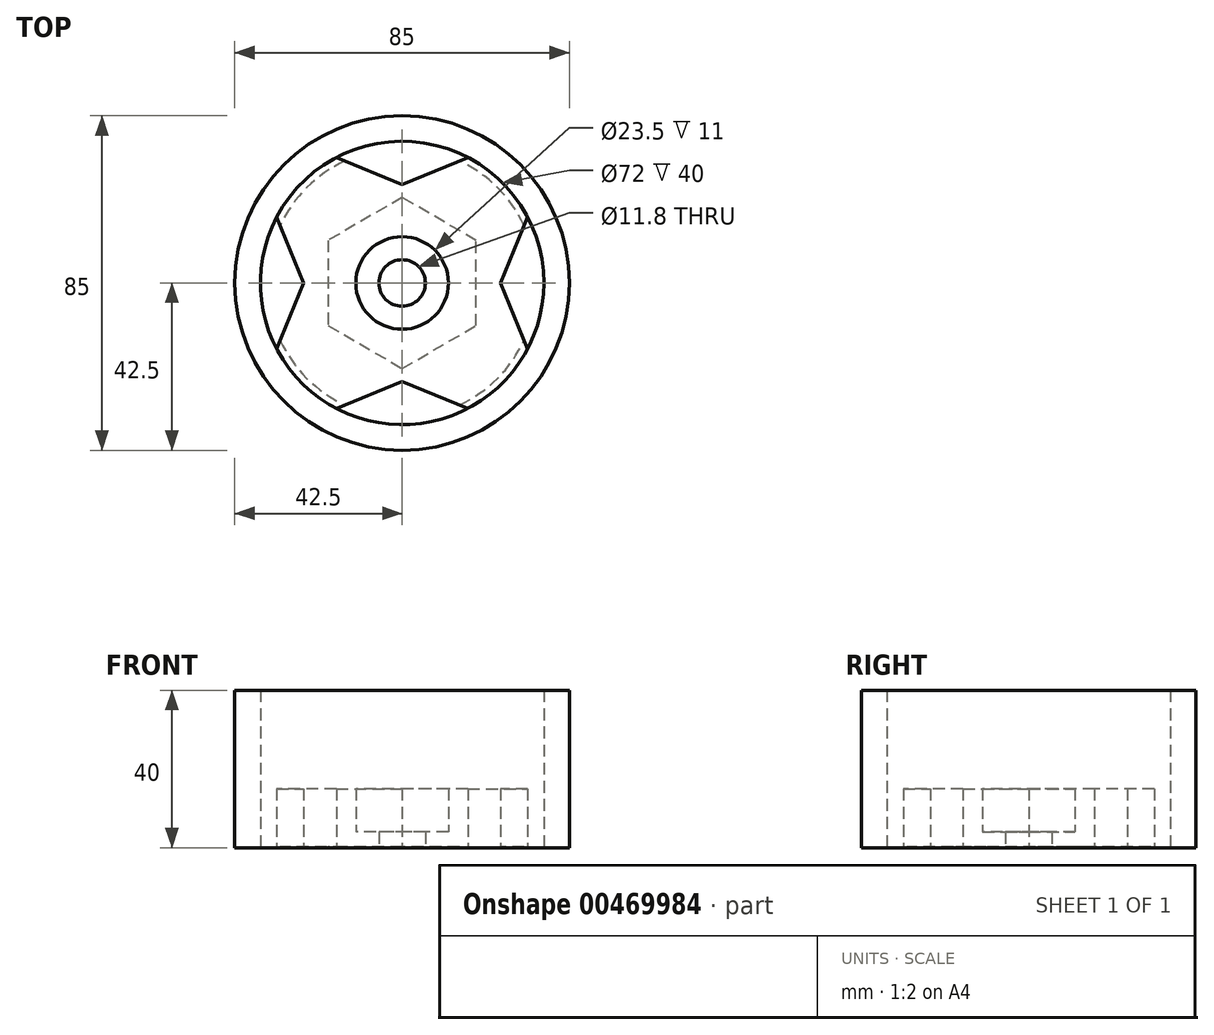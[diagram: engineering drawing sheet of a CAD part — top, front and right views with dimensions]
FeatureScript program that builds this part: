
annotation { "Feature Type Name" : "Feature", "Feature Type Description" : "" }
export const myFeature = defineFeature(function(context is Context, id is Id, definition is map)
    precondition{}
    {
        {
            var Q0;
            Q0=qCreatedBy(makeId("Top.planeOp"),FACE);
            var sketch = newSketch(context, id + "F0", { "sketchPlane" : qUnion([Q0])});
            skCircle(sketch, "E0", {"center": v(0, 0) * mm, "radius": 5.9 * mm});
            skCircle(sketch, "E1", {"center": v(0, 0) * mm, "radius": 11.75 * mm});
            skLineSegment(sketch, "E2.bottom", {"start": v(-42.5, 42.5) * mm, "end": v(42.5, 42.5) * mm, "construction": true});
            skLineSegment(sketch, "E2.top", {"start": v(-42.5, -42.5) * mm, "end": v(42.5, -42.5) * mm, "construction": true});
            skLineSegment(sketch, "E2.left", {"start": v(-42.5, 42.5) * mm, "end": v(-42.5, -42.5) * mm, "construction": true});
            skLineSegment(sketch, "E2.right", {"start": v(42.5, 42.5) * mm, "end": v(42.5, -42.5) * mm, "construction": true});
            skCircle(sketch, "E3.cCircle", {"center": v(0, 0) * mm, "radius": 25 * mm, "construction": true});
            skLineSegment(sketch, "E3.0", {"start": v(-10.35, 25) * mm, "end": v(10.35, 25) * mm, "construction": true});
            skLineSegment(sketch, "E3.1", {"start": v(10.35, 25) * mm, "end": v(25, 10.35) * mm, "construction": true});
            skLineSegment(sketch, "E3.2", {"start": v(25, 10.35) * mm, "end": v(25, -10.35) * mm, "construction": true});
            skLineSegment(sketch, "E3.3", {"start": v(25, -10.35) * mm, "end": v(10.35, -25) * mm, "construction": true});
            skLineSegment(sketch, "E3.4", {"start": v(10.35, -25) * mm, "end": v(-10.35, -25) * mm, "construction": true});
            skLineSegment(sketch, "E3.5", {"start": v(-10.35, -25) * mm, "end": v(-25, -10.35) * mm, "construction": true});
            skLineSegment(sketch, "E3.6", {"start": v(-25, -10.35) * mm, "end": v(-25, 10.35) * mm, "construction": true});
            skLineSegment(sketch, "E3.7", {"start": v(-25, 10.35) * mm, "end": v(-10.35, 25) * mm, "construction": true});
            skPoint(sketch, "E3.0.midPoint", {"position": v(0, 25) * mm});
            skLineSegment(sketch, "E4", {"start": v(-42.5, -42.5) * mm, "end": v(-25, 0) * mm});
            skLineSegment(sketch, "E5", {"start": v(-25, 0) * mm, "end": v(-42.5, 42.5) * mm});
            skLineSegment(sketch, "E6", {"start": v(-42.5, 42.5) * mm, "end": v(0, 25) * mm});
            skLineSegment(sketch, "E7", {"start": v(0, 25) * mm, "end": v(42.5, 42.5) * mm});
            skLineSegment(sketch, "E8", {"start": v(42.5, 42.5) * mm, "end": v(25, 0) * mm});
            skLineSegment(sketch, "E9", {"start": v(25, 0) * mm, "end": v(42.5, -42.5) * mm});
            skLineSegment(sketch, "E10", {"start": v(42.5, -42.5) * mm, "end": v(0, -25) * mm});
            skLineSegment(sketch, "E11", {"start": v(0, -25) * mm, "end": v(-42.5, -42.5) * mm});
            skCircle(sketch, "E12", {"center": v(0, 0) * mm, "radius": 42.5 * mm});
            skCircle(sketch, "E13", {"center": v(0, 0) * mm, "radius": 40 * mm});
            skCircle(sketch, "E14", {"center": v(0, 0) * mm, "radius": 36 * mm});
            skSolve(sketch);
        }
        {
            var Q0;
            {var subQ0=sQuery(id+"F0.wireOp",EDGE,"E12");var subQ1=sQuery(id+"F0.wireOp",EDGE,"E4");var subQ2=makeQuery(id+"F0.imprint","INTERSECT",VERTEX,{"derivedFrom":[subQ1,subQ0]});Q0=makeQuery(id+"F0.imprint","IMPRINT",FACE,{"disambiguationData":[TD([[makeQuery(id+"F0.imprint","IMPRINT",EDGE,{"disambiguationData":[TD([[subQ2,-1.0]])],"derivedFrom":subQ1}),1.0]])]});}
            var Q1;
            {var subQ0=sQuery(id+"F0.wireOp",EDGE,"E12");var subQ1=sQuery(id+"F0.wireOp",EDGE,"E5");var subQ2=makeQuery(id+"F0.imprint","INTERSECT",VERTEX,{"derivedFrom":[subQ1,subQ0]});Q1=makeQuery(id+"F0.imprint","IMPRINT",FACE,{"disambiguationData":[TD([[makeQuery(id+"F0.imprint","IMPRINT",EDGE,{"disambiguationData":[TD([[subQ2,1.0]])],"derivedFrom":subQ1}),-1.0]])]});}
            var Q2;
            {var subQ0=sQuery(id+"F0.wireOp",EDGE,"E12");var subQ1=sQuery(id+"F0.wireOp",EDGE,"E6");var subQ2=makeQuery(id+"F0.imprint","INTERSECT",VERTEX,{"derivedFrom":[subQ1,subQ0]});Q2=makeQuery(id+"F0.imprint","IMPRINT",FACE,{"disambiguationData":[TD([[makeQuery(id+"F0.imprint","IMPRINT",EDGE,{"disambiguationData":[TD([[subQ2,-1.0]])],"derivedFrom":subQ1}),1.0]])]});}
            var Q3;
            {var subQ0=sQuery(id+"F0.wireOp",EDGE,"E12");var subQ1=sQuery(id+"F0.wireOp",EDGE,"E7");var subQ2=makeQuery(id+"F0.imprint","INTERSECT",VERTEX,{"derivedFrom":[subQ1,subQ0]});Q3=makeQuery(id+"F0.imprint","IMPRINT",FACE,{"disambiguationData":[TD([[makeQuery(id+"F0.imprint","IMPRINT",EDGE,{"disambiguationData":[TD([[subQ2,1.0]])],"derivedFrom":subQ1}),-1.0]])]});}
            var Q4;
            {var subQ0=sQuery(id+"F0.wireOp",EDGE,"E12");var subQ1=sQuery(id+"F0.wireOp",EDGE,"E8");var subQ2=makeQuery(id+"F0.imprint","INTERSECT",VERTEX,{"derivedFrom":[subQ1,subQ0]});Q4=makeQuery(id+"F0.imprint","IMPRINT",FACE,{"disambiguationData":[TD([[makeQuery(id+"F0.imprint","IMPRINT",EDGE,{"disambiguationData":[TD([[subQ2,-1.0]])],"derivedFrom":subQ1}),1.0]])]});}
            var Q5;
            {var subQ0=sQuery(id+"F0.wireOp",EDGE,"E12");var subQ1=sQuery(id+"F0.wireOp",EDGE,"E9");var subQ2=makeQuery(id+"F0.imprint","INTERSECT",VERTEX,{"derivedFrom":[subQ1,subQ0]});Q5=makeQuery(id+"F0.imprint","IMPRINT",FACE,{"disambiguationData":[TD([[makeQuery(id+"F0.imprint","IMPRINT",EDGE,{"disambiguationData":[TD([[subQ2,1.0]])],"derivedFrom":subQ1}),-1.0]])]});}
            var Q6;
            {var subQ0=sQuery(id+"F0.wireOp",EDGE,"E12");var subQ1=sQuery(id+"F0.wireOp",EDGE,"E10");var subQ2=makeQuery(id+"F0.imprint","INTERSECT",VERTEX,{"derivedFrom":[subQ1,subQ0]});Q6=makeQuery(id+"F0.imprint","IMPRINT",FACE,{"disambiguationData":[TD([[makeQuery(id+"F0.imprint","IMPRINT",EDGE,{"disambiguationData":[TD([[subQ2,-1.0]])],"derivedFrom":subQ1}),1.0]])]});}
            var Q7;
            {var subQ0=sQuery(id+"F0.wireOp",EDGE,"E12");var subQ1=sQuery(id+"F0.wireOp",EDGE,"E4");var subQ2=makeQuery(id+"F0.imprint","INTERSECT",VERTEX,{"derivedFrom":[subQ1,subQ0]});Q7=makeQuery(id+"F0.imprint","IMPRINT",FACE,{"disambiguationData":[TD([[makeQuery(id+"F0.imprint","IMPRINT",EDGE,{"disambiguationData":[TD([[subQ2,-1.0]])],"derivedFrom":subQ1}),-1.0]])]});}
            var Q8;
            Q8=makeQuery(id+"F0.imprint","IMPRINT",FACE,{"disambiguationData":[TD([[makeQuery(id+"F0.imprint","IMPRINT",EDGE,{"derivedFrom":sQuery(id+"F0.wireOp",EDGE,"E1")}),-1.0]])]});
            var Q9;
            {var subQ0=sQuery(id+"F0.wireOp",EDGE,"E14");var subQ1=sQuery(id+"F0.wireOp",EDGE,"E5");var subQ2=makeQuery(id+"F0.imprint","INTERSECT",VERTEX,{"derivedFrom":[subQ1,subQ0]});Q9=makeQuery(id+"F0.imprint","IMPRINT",FACE,{"disambiguationData":[TD([[makeQuery(id+"F0.imprint","IMPRINT",EDGE,{"disambiguationData":[TD([[subQ2,-1.0]])],"derivedFrom":subQ1}),-1.0]])]});}
            var Q10;
            {var subQ0=sQuery(id+"F0.wireOp",EDGE,"E14");var subQ1=sQuery(id+"F0.wireOp",EDGE,"E7");var subQ2=makeQuery(id+"F0.imprint","INTERSECT",VERTEX,{"derivedFrom":[subQ1,subQ0]});Q10=makeQuery(id+"F0.imprint","IMPRINT",FACE,{"disambiguationData":[TD([[makeQuery(id+"F0.imprint","IMPRINT",EDGE,{"disambiguationData":[TD([[subQ2,-1.0]])],"derivedFrom":subQ1}),-1.0]])]});}
            var Q11;
            {var subQ0=sQuery(id+"F0.wireOp",EDGE,"E13");var subQ1=sQuery(id+"F0.wireOp",EDGE,"E4");var subQ2=makeQuery(id+"F0.imprint","INTERSECT",VERTEX,{"derivedFrom":[subQ1,subQ0]});Q11=makeQuery(id+"F0.imprint","IMPRINT",FACE,{"disambiguationData":[TD([[makeQuery(id+"F0.imprint","IMPRINT",EDGE,{"disambiguationData":[TD([[subQ2,-1.0]])],"derivedFrom":subQ1}),-1.0]])]});}
            var Q12;
            {var subQ0=sQuery(id+"F0.wireOp",EDGE,"E14");var subQ1=sQuery(id+"F0.wireOp",EDGE,"E9");var subQ2=makeQuery(id+"F0.imprint","INTERSECT",VERTEX,{"derivedFrom":[subQ1,subQ0]});Q12=makeQuery(id+"F0.imprint","IMPRINT",FACE,{"disambiguationData":[TD([[makeQuery(id+"F0.imprint","IMPRINT",EDGE,{"disambiguationData":[TD([[subQ2,-1.0]])],"derivedFrom":subQ1}),-1.0]])]});}
            var Q13;
            {var subQ0=sQuery(id+"F0.wireOp",EDGE,"E13");var subQ1=sQuery(id+"F0.wireOp",EDGE,"E4");var subQ2=makeQuery(id+"F0.imprint","INTERSECT",VERTEX,{"derivedFrom":[subQ1,subQ0]});Q13=makeQuery(id+"F0.imprint","IMPRINT",FACE,{"disambiguationData":[TD([[makeQuery(id+"F0.imprint","IMPRINT",EDGE,{"disambiguationData":[TD([[subQ2,-1.0]])],"derivedFrom":subQ1}),1.0]])]});}
            var Q14;
            {var subQ0=sQuery(id+"F0.wireOp",EDGE,"E13");var subQ1=sQuery(id+"F0.wireOp",EDGE,"E6");var subQ2=makeQuery(id+"F0.imprint","INTERSECT",VERTEX,{"derivedFrom":[subQ1,subQ0]});Q14=makeQuery(id+"F0.imprint","IMPRINT",FACE,{"disambiguationData":[TD([[makeQuery(id+"F0.imprint","IMPRINT",EDGE,{"disambiguationData":[TD([[subQ2,-1.0]])],"derivedFrom":subQ1}),1.0]])]});}
            var Q15;
            {var subQ0=sQuery(id+"F0.wireOp",EDGE,"E13");var subQ1=sQuery(id+"F0.wireOp",EDGE,"E8");var subQ2=makeQuery(id+"F0.imprint","INTERSECT",VERTEX,{"derivedFrom":[subQ1,subQ0]});Q15=makeQuery(id+"F0.imprint","IMPRINT",FACE,{"disambiguationData":[TD([[makeQuery(id+"F0.imprint","IMPRINT",EDGE,{"disambiguationData":[TD([[subQ2,-1.0]])],"derivedFrom":subQ1}),1.0]])]});}
            var Q16;
            {var subQ0=sQuery(id+"F0.wireOp",EDGE,"E13");var subQ1=sQuery(id+"F0.wireOp",EDGE,"E10");var subQ2=makeQuery(id+"F0.imprint","INTERSECT",VERTEX,{"derivedFrom":[subQ1,subQ0]});Q16=makeQuery(id+"F0.imprint","IMPRINT",FACE,{"disambiguationData":[TD([[makeQuery(id+"F0.imprint","IMPRINT",EDGE,{"disambiguationData":[TD([[subQ2,-1.0]])],"derivedFrom":subQ1}),1.0]])]});}
            extrude(context, id + "F1", {"entities" : qUnion([Q0, Q1, Q2, Q3, Q4, Q5, Q6, Q7, Q8, Q9, Q10, Q11, Q12, Q13, Q14, Q15, Q16]), "depth" : 40 * mm});
        }
        {
            var Q0;
            Q0=makeQuery(id+"F1.opExtrude","CAP_FACE",FACE,{"disambiguationData":[OSD([sQuery(id+"F0.wireOp",EDGE,"E1"),sQuery(id+"F0.wireOp",EDGE,"E4"),sQuery(id+"F0.wireOp",EDGE,"E5"),sQuery(id+"F0.wireOp",EDGE,"E6"),sQuery(id+"F0.wireOp",EDGE,"E7"),sQuery(id+"F0.wireOp",EDGE,"E8"),sQuery(id+"F0.wireOp",EDGE,"E9"),sQuery(id+"F0.wireOp",EDGE,"E10"),sQuery(id+"F0.wireOp",EDGE,"E11"),sQuery(id+"F0.wireOp",EDGE,"E12"),sQuery(id+"F0.wireOp",EDGE,"E13")])],"isStart":false});
            var sketch = newSketch(context, id + "F2", { "sketchPlane" : qUnion([Q0])});
            skCircle(sketch, "E15", {"center": v(0, 0) * mm, "radius": 36 * mm});
            skSolve(sketch);
        }
        {
            var Q0;
            Q0 = qSketchRegion(id + "F2", true);
            extrude(context, id + "F3", {"entities" : qUnion([Q0]), "operationType" : NewBodyOperationType.REMOVE, "oppositeDirection" : true, "depth" : 25 * mm});
        }
        {
            var Q0;
            Q0=makeQuery(id+"F1.opExtrude","CAP_FACE",FACE,{"disambiguationData":[OSD([sQuery(id+"F0.wireOp",EDGE,"E1"),sQuery(id+"F0.wireOp",EDGE,"E4"),sQuery(id+"F0.wireOp",EDGE,"E5"),sQuery(id+"F0.wireOp",EDGE,"E6"),sQuery(id+"F0.wireOp",EDGE,"E7"),sQuery(id+"F0.wireOp",EDGE,"E8"),sQuery(id+"F0.wireOp",EDGE,"E9"),sQuery(id+"F0.wireOp",EDGE,"E10"),sQuery(id+"F0.wireOp",EDGE,"E11"),sQuery(id+"F0.wireOp",EDGE,"E12"),sQuery(id+"F0.wireOp",EDGE,"E14")])],"isStart":true});
            var sketch = newSketch(context, id + "F4", { "sketchPlane" : qUnion([Q0])});
            skCircle(sketch, "E16", {"center": v(0, 0) * mm, "radius": 34.25 * mm});
            skCircle(sketch, "E17.cCircle", {"center": v(0, 0) * mm, "radius": 18.78 * mm, "construction": true});
            skLineSegment(sketch, "E17.0", {"start": v(-18.78, -10.84) * mm, "end": v(-18.78, 10.84) * mm});
            skLineSegment(sketch, "E17.1", {"start": v(-18.78, 10.84) * mm, "end": v(0, 21.69) * mm});
            skLineSegment(sketch, "E17.2", {"start": v(0, 21.69) * mm, "end": v(18.78, 10.84) * mm});
            skLineSegment(sketch, "E17.3", {"start": v(18.78, 10.84) * mm, "end": v(18.78, -10.84) * mm});
            skLineSegment(sketch, "E17.4", {"start": v(18.78, -10.84) * mm, "end": v(0, -21.69) * mm});
            skLineSegment(sketch, "E17.5", {"start": v(0, -21.69) * mm, "end": v(-18.78, -10.84) * mm});
            skPoint(sketch, "E17.0.midPoint", {"position": v(-18.78, 0) * mm});
            skSolve(sketch);
        }
        {
            var Q0;
            Q0=makeQuery(id+"F4.imprint","IMPRINT",FACE,{"disambiguationData":[TD([[makeQuery(id+"F4.imprint","IMPRINT",EDGE,{"derivedFrom":sQuery(id+"F4.wireOp",EDGE,"E17.0")}),1.0]])]});
            extrude(context, id + "F5", {"entities" : qUnion([Q0]), "operationType" : NewBodyOperationType.REMOVE, "oppositeDirection" : true, "depth" : 0.2 * mm});
        }
        {
            var Q0;
            Q0=qCreatedBy(makeId("Top.planeOp"),FACE);
            var sketch = newSketch(context, id + "F6", { "sketchPlane" : qUnion([Q0])});
            skCircle(sketch, "E18", {"center": v(0, 0) * mm, "radius": 11.75 * mm});
            skCircle(sketch, "E19", {"center": v(0, 0) * mm, "radius": 5.9 * mm});
            skSolve(sketch);
        }
        {
            var Q0;
            Q0=makeQuery(id+"F6.imprint","IMPRINT",FACE,{"disambiguationData":[TD([[makeQuery(id+"F6.imprint","IMPRINT",EDGE,{"derivedFrom":sQuery(id+"F6.wireOp",EDGE,"E18")}),1.0]])]});
            extrude(context, id + "F7", {"entities" : qUnion([Q0]), "operationType" : NewBodyOperationType.ADD, "depth" : 4 * mm});
        }
    });
